# Revit family: Faucet-Lavatory-KOHLER-Artifacts_Bell-K-72759
name_source: partatom
category: Plumbing Fixtures
units: mm (PartAtom-declared; Revit-internal decimal feet)

## family parameters
Cut with Voids When Loaded = No
Host = Face
OmniClass Number = 23.45.55.00
OmniClass Title = Sanitary Faucets, Wastes
Part Type = Normal
Room Calculation Point = No
Round Connector Dimension = Use Diameter
Shared = No

## types (1)
- Not a Type-See Type Catalog
    ADA Compliant = No
    Assembly Code = D2010
    CW Connection = Yes
    Cold Water Inlet = Cold Water Inlet
    Date Modified = 10/02/2018
    Default Elevation = 36"
    Description = Bathroom sink spout
    Drain Included = Yes
    Edition number = 1
    Faucet Hole Spacing = 0"
    Finish = Default
    Flow Rate = 1 GPM
    HW Connection = Yes
    Handle Clearance = 0"
    Height = 4 11/16"
    Hot Water Inlet = Hot Water Inlet
    Length = 5 3/8"
    Manufacturer = KOHLER Co.
    MasterFormat 1995 = 15410
    MasterFormat 2004 = 22.41.39
    Material = Metal Construction
    Pressure = 60.00 psi
    Product Documentation Link = http://www.us.kohler.com
    Product Guid = 92a9f111-44d4-44fb-9ba6-0d35c329e498
    Product Name = Artifacts
    Product Page URL = http://www.us.kohler.com
    Product data url = https://bimobject.com
    Spout Reach = 5 3/8"
    Type = 0
    URL = https://www.us.kohler.com
    Vent Connection = No
    Waste Connection = No
    Waste Water Outlet = Waste Water Outlet
    Width = 2 11/16"

## geometry (parser evidence)
native form markers: Sweep x4
no freeform markers — native parametric forms only
